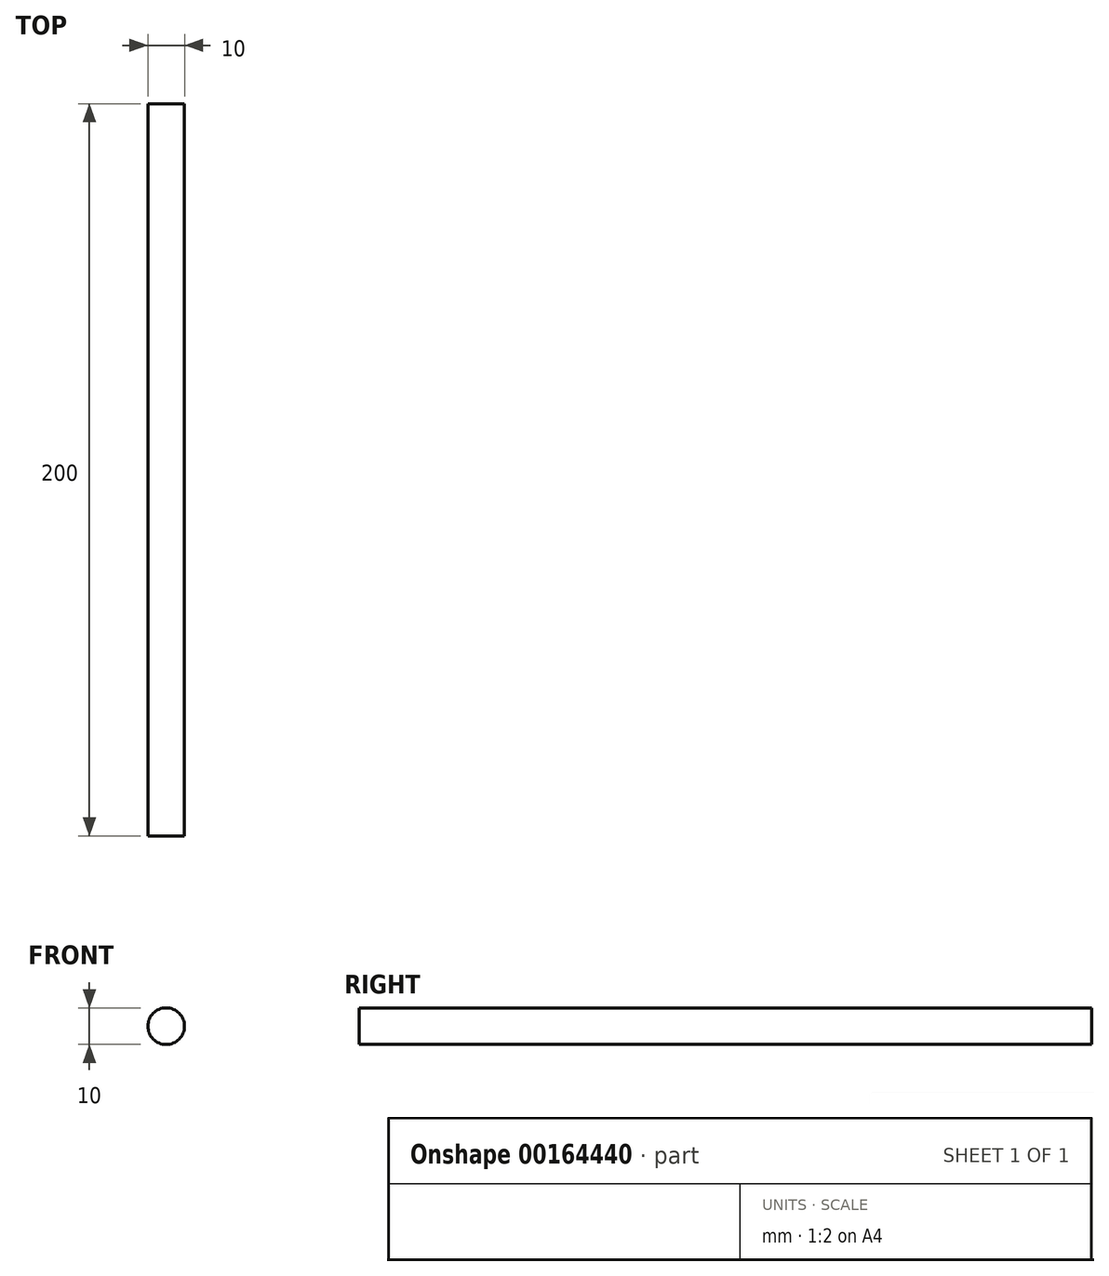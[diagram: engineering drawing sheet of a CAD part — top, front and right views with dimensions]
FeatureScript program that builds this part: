
annotation { "Feature Type Name" : "Feature", "Feature Type Description" : "" }
export const myFeature = defineFeature(function(context is Context, id is Id, definition is map)
    precondition{}
    {
        {
            var Q0;
            Q0=qCreatedBy(makeId("Front.planeOp"),FACE);
            var sketch = newSketch(context, id + "F0", { "sketchPlane" : qUnion([Q0])});
            skCircle(sketch, "E0", {"center": v(-48.82, 20.87) * mm, "radius": 5 * mm});
            skSolve(sketch);
        }
        {
            var Q0;
            Q0=makeQuery(id+"F0.imprint","IMPRINT",FACE,{"disambiguationData":[TD([[makeQuery(id+"F0.imprint","IMPRINT",EDGE,{"derivedFrom":sQuery(id+"F0.wireOp",EDGE,"E0")}),1.0]])]});
            extrude(context, id + "F1", {"entities" : qUnion([Q0]), "depth" : 200 * mm});
        }
    });
